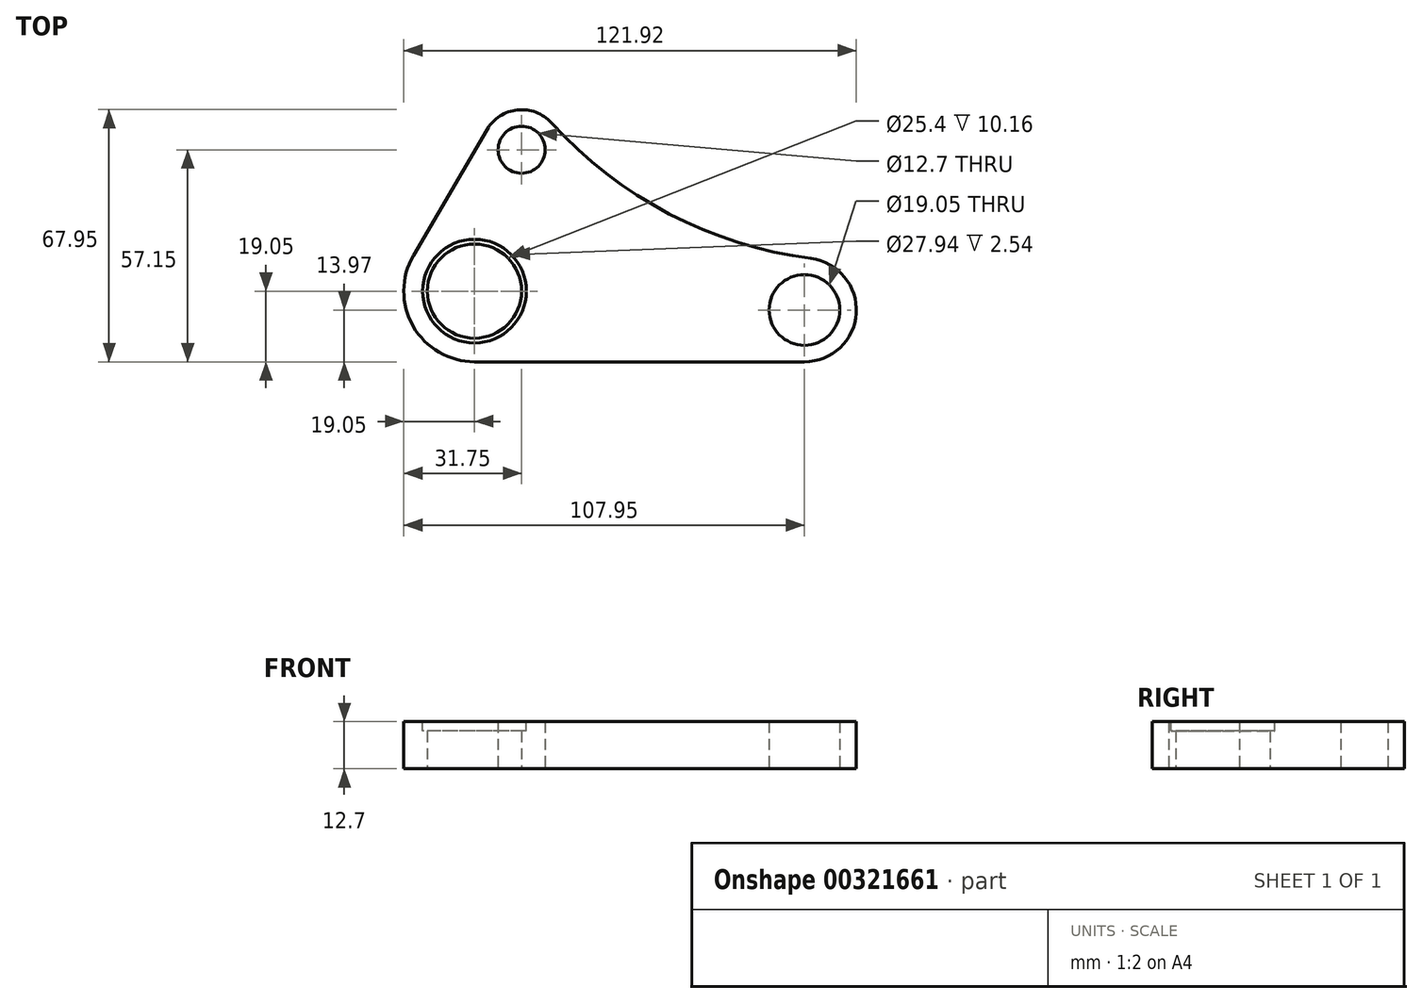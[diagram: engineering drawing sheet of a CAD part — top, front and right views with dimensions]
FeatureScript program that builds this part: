
annotation { "Feature Type Name" : "Feature", "Feature Type Description" : "" }
export const myFeature = defineFeature(function(context is Context, id is Id, definition is map)
    precondition{}
    {
        {
            var Q0;
            Q0=qCreatedBy(makeId("Top.planeOp"),FACE);
            var sketch = newSketch(context, id + "F0", { "sketchPlane" : qUnion([Q0])});
            skCircle(sketch, "E0", {"center": v(0, 0) * mm, "radius": 12.7 * mm});
            skCircle(sketch, "E1", {"center": v(12.7, 38.1) * mm, "radius": 6.35 * mm});
            skCircle(sketch, "E2", {"center": v(88.9, -5.08) * mm, "radius": 9.53 * mm});
            skArc(sketch, "E3", {"start": v(-16.45, 9.61) * mm, "mid": v(-16.52, -9.48) * mm, "end": v(0, -19.05) * mm});
            skArc(sketch, "E4", {"start": v(20.7, 45.35) * mm, "mid": v(11.58, 48.84) * mm, "end": v(3.38, 43.55) * mm});
            skArc(sketch, "E5", {"start": v(88.9, -19.05) * mm, "mid": v(102.84, -5.98) * mm, "end": v(90.7, 8.77) * mm});
            skLineSegment(sketch, "E6", {"start": v(0, -19.05) * mm, "end": v(88.9, -19.05) * mm});
            skArc(sketch, "E7", {"start": v(20.7, 45.35) * mm, "mid": v(52.44, 20.83) * mm, "end": v(90.7, 8.77) * mm});
            skLineSegment(sketch, "E8", {"start": v(-16.45, 9.61) * mm, "end": v(3.38, 43.55) * mm});
            skLineSegment(sketch, "E9", {"start": v(3.38, 43.55) * mm, "end": v(20.7, 45.35) * mm, "construction": true});
            skLineSegment(sketch, "E10", {"start": v(90.7, 8.77) * mm, "end": v(88.9, -19.05) * mm, "construction": true});
            skLineSegment(sketch, "E11", {"start": v(-16.45, 9.61) * mm, "end": v(0, -19.05) * mm, "construction": true});
            skSolve(sketch);
        }
        {
            var Q0;
            Q0 = qSketchRegion(id + "F0", true);
            extrude(context, id + "F1", {"entities" : qUnion([Q0]), "endBound" : BoundingType.SYMMETRIC, "depth" : 12.7 * mm});
        }
        {
            var Q0;
            Q0=makeQuery(id+"F1.opExtrude","CAP_FACE",FACE,{"disambiguationData":[OSD([sQuery(id+"F0.wireOp",EDGE,"E0"),sQuery(id+"F0.wireOp",EDGE,"E1"),sQuery(id+"F0.wireOp",EDGE,"E2"),sQuery(id+"F0.wireOp",EDGE,"E3"),sQuery(id+"F0.wireOp",EDGE,"E4"),sQuery(id+"F0.wireOp",EDGE,"E5"),sQuery(id+"F0.wireOp",EDGE,"E6"),sQuery(id+"F0.wireOp",EDGE,"E7"),sQuery(id+"F0.wireOp",EDGE,"E8")])],"isStart":false});
            var sketch = newSketch(context, id + "F2", { "sketchPlane" : qUnion([Q0])});
            skCircle(sketch, "E12", {"center": v(0, 0) * mm, "radius": 13.97 * mm});
            skSolve(sketch);
        }
        {
            var Q0;
            Q0 = qSketchRegion(id + "F2", true);
            extrude(context, id + "F3", {"entities" : qUnion([Q0]), "operationType" : NewBodyOperationType.REMOVE, "oppositeDirection" : true, "depth" : 2.54 * mm});
        }
    });
